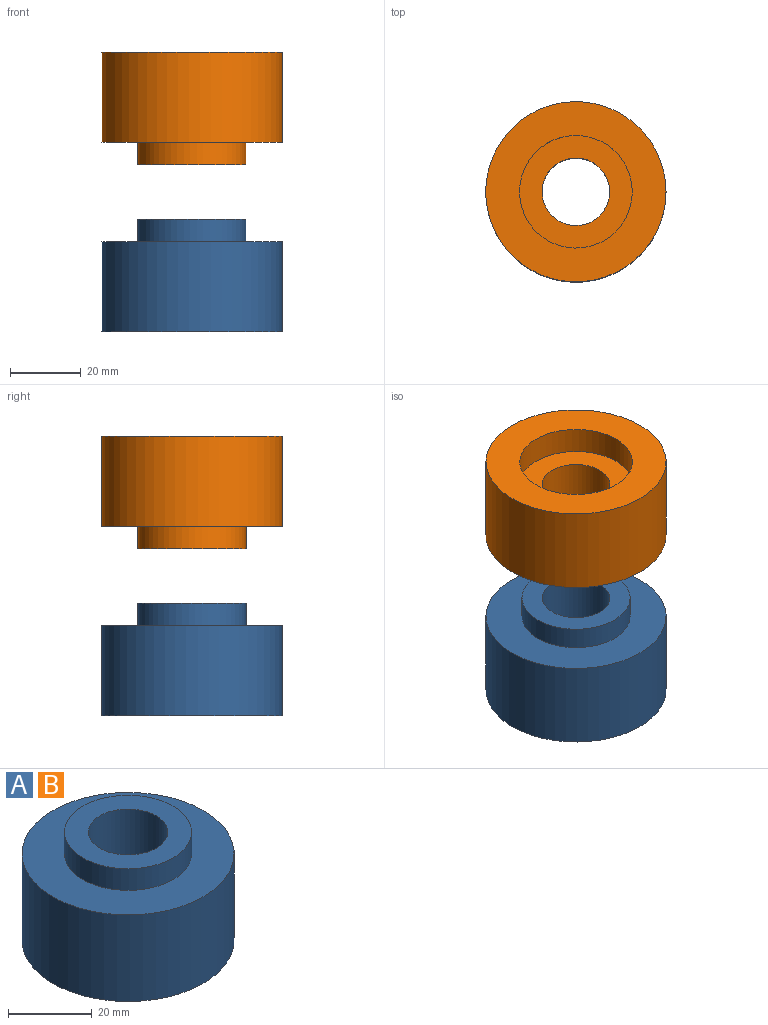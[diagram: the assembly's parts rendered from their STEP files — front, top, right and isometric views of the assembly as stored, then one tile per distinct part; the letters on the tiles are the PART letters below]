
ASSEMBLY  parts=2 mates=2
PART A: 8 faces, bbox 50.8x50.8x31.8 mm
  f0: cylinder r=9.53mm len=24.13mm, axis (0,0,-1), area 1444.1mm2, adj f5,f7
  f1: cylinder r=25.4mm len=50.8mm, axis (0,0,-1), area 4053.7mm2, adj f2,f3
  f2: plane 50.8x50.8mm, normal (0,0,1), area 1297.2mm2, adj f1,f6
  f3: plane 50.8x50.8mm, normal (0,0,-1), area 1235.1mm2, adj f1,f4
  f4: cylinder r=15.88mm len=31.75mm, axis (0,0,-1), area 760.1mm2, adj f3,f5
  f5: plane 31.75x31.75mm, normal (0,0,-1), area 506.7mm2, adj f0,f4
  f6: cylinder r=15.24mm len=30.48mm, axis (0,0,-1), area 608mm2, adj f2,f7
  f7: plane 30.48x30.48mm, normal (0,0,1), area 444.6mm2, adj f0,f6
PART B: same geometry as A
PLACE A t=(-1.81,2.2,-64.34)mm fixed
PLACE B rot(axis=(1,0,0),180deg) t=(-1.81,2.2,14.4)mm
MATE cylindrical B.f1 <-> A.f1  axis (0,0,1) through (-1.81,2.2,1.7)mm
MATE planar B.f6 <-> A.f6  axis (0,0,-1) through (-1.81,2.2,-17.35)mm
